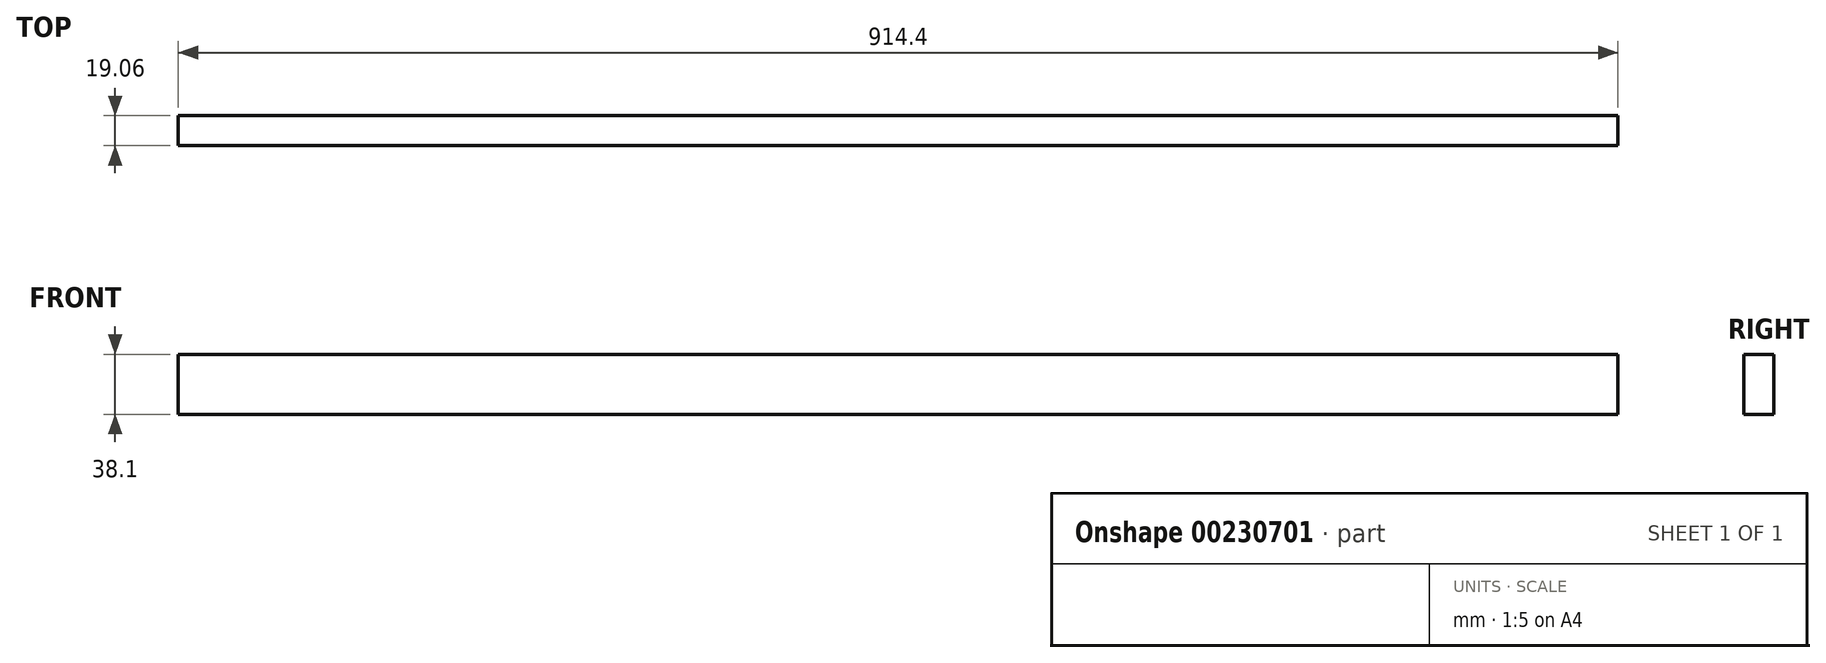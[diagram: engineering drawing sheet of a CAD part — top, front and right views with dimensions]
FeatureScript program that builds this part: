
annotation { "Feature Type Name" : "Feature", "Feature Type Description" : "" }
export const myFeature = defineFeature(function(context is Context, id is Id, definition is map)
    precondition{}
    {
        {
            var Q0;
            Q0=qCreatedBy(makeId("Right.planeOp"),FACE);
            var sketch = newSketch(context, id + "F0", { "sketchPlane" : qUnion([Q0])});
            skLineSegment(sketch, "E0.bottom", {"start": v(-9.52, 19.05) * mm, "end": v(9.53, 19.05) * mm});
            skLineSegment(sketch, "E0.top", {"start": v(-9.52, -19.05) * mm, "end": v(9.53, -19.05) * mm});
            skLineSegment(sketch, "E0.left", {"start": v(-9.52, 19.05) * mm, "end": v(-9.52, -19.05) * mm});
            skLineSegment(sketch, "E0.right", {"start": v(9.53, 19.05) * mm, "end": v(9.53, -19.05) * mm});
            skSolve(sketch);
        }
        {
            var Q0;
            Q0=makeQuery(id+"F0.imprint","IMPRINT",FACE,{"disambiguationData":[TD([[makeQuery(id+"F0.imprint","IMPRINT",EDGE,{"derivedFrom":sQuery(id+"F0.wireOp",EDGE,"E0.bottom")}),-1.0]])]});
            extrude(context, id + "F1", {"entities" : qUnion([Q0]), "depth" : 914.4 * mm});
        }
    });
